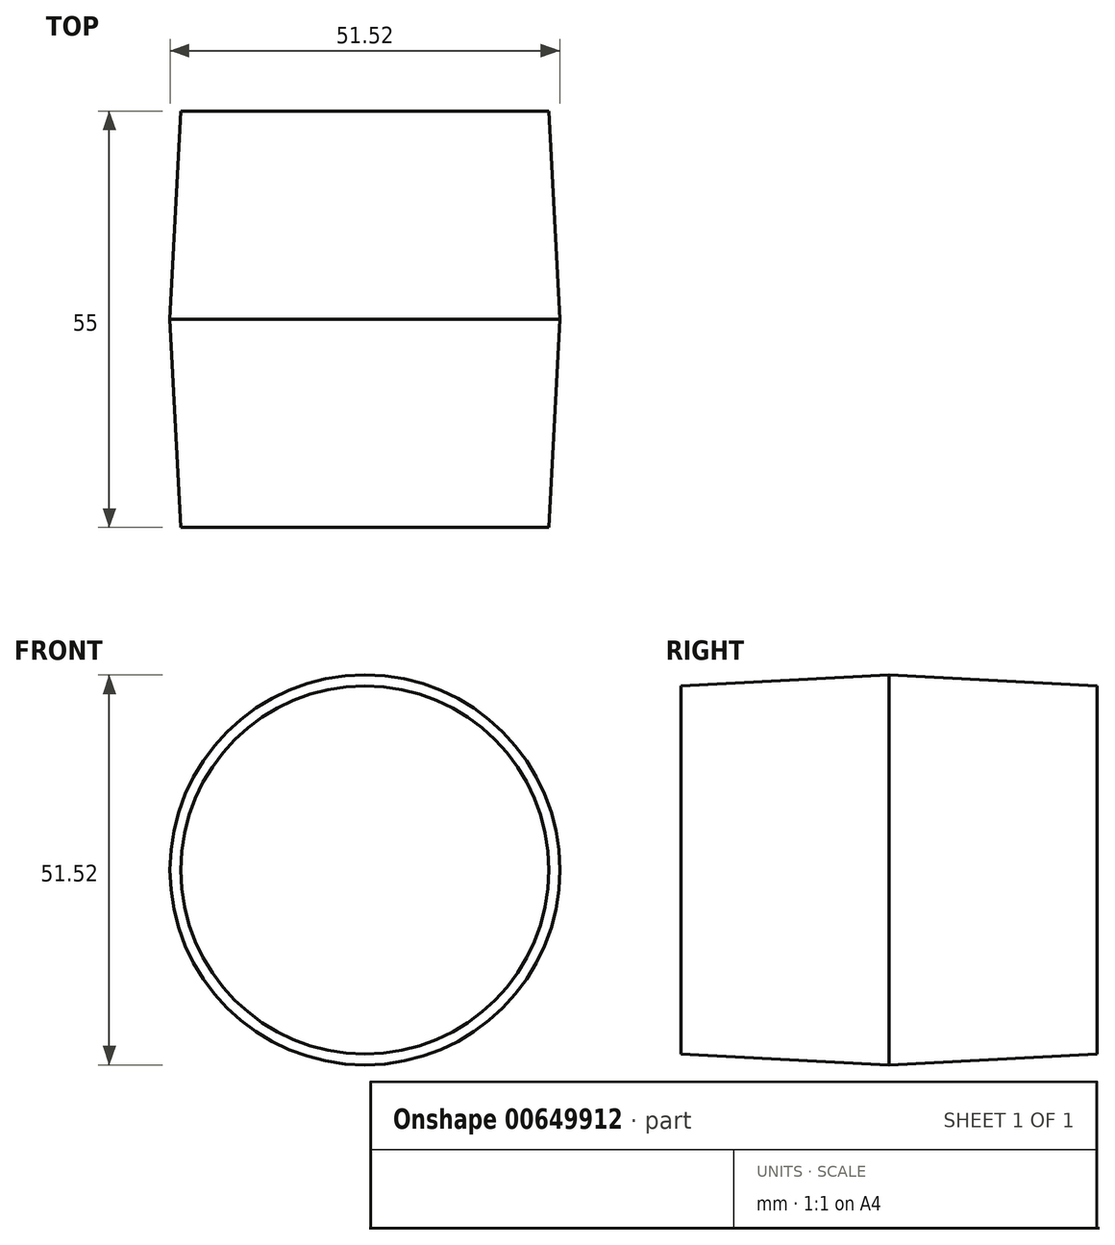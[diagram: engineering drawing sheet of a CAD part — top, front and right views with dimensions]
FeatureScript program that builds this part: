
annotation { "Feature Type Name" : "Feature", "Feature Type Description" : "" }
export const myFeature = defineFeature(function(context is Context, id is Id, definition is map)
    precondition{}
    {
        {
            var Q0;
            Q0=qCreatedBy(makeId("Front.planeOp"),FACE);
            var sketch = newSketch(context, id + "F0", { "sketchPlane" : qUnion([Q0])});
            skCircle(sketch, "E0", {"center": v(0, 12.79) * mm, "radius": 25.76 * mm});
            skSolve(sketch);
        }
        {
            var Q0;
            Q0 = qSketchRegion(id + "F0", true);
            extrude(context, id + "F1", {"entities" : qUnion([Q0]), "endBound" : BoundingType.SYMMETRIC, "depth" : 55 * mm, "offsetDistance" : 25.4 * mm, "hasDraft" : true, "draftAngle" : 3 * degree, "draftPullDirection" : true});
        }
    });
